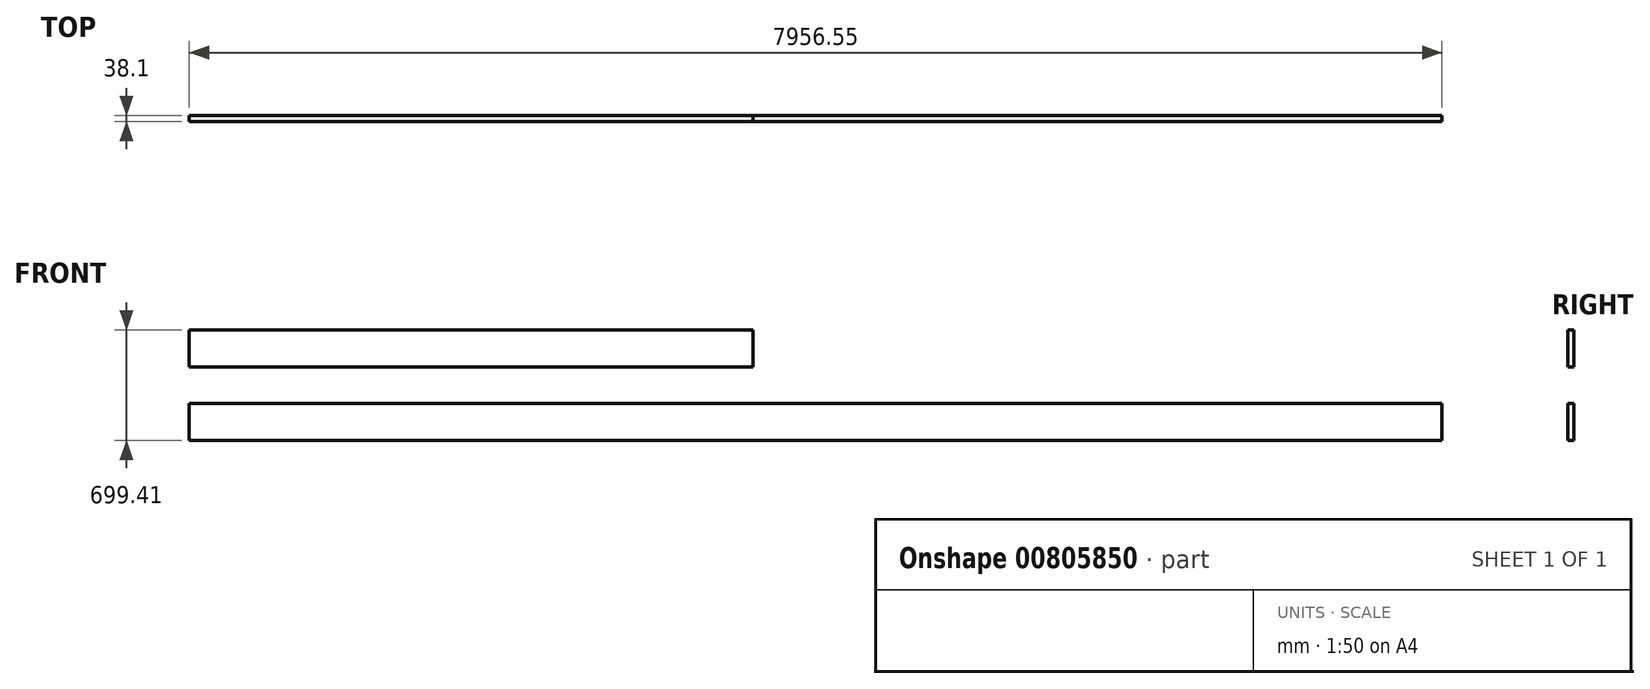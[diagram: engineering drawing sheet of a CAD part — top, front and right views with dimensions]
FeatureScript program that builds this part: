
annotation { "Feature Type Name" : "Feature", "Feature Type Description" : "" }
export const myFeature = defineFeature(function(context is Context, id is Id, definition is map)
    precondition{}
    {
        {
            var Q0;
            Q0=qCreatedBy(makeId("Front.planeOp"),FACE);
            var sketch = newSketch(context, id + "F0", { "sketchPlane" : qUnion([Q0])});
            skLineSegment(sketch, "E0.bottom", {"start": v(3581.4, 234.95) * mm, "end": v(0, 234.95) * mm});
            skLineSegment(sketch, "E0.top", {"start": v(3581.4, 0) * mm, "end": v(0, 0) * mm});
            skLineSegment(sketch, "E0.left", {"start": v(3581.4, 234.95) * mm, "end": v(3581.4, 0) * mm});
            skLineSegment(sketch, "E0.right", {"start": v(0, 234.95) * mm, "end": v(0, 0) * mm});
            skSolve(sketch);
        }
        {
            var Q0;
            Q0=qSketchRegion(id+"F0",true);
            extrude(context, id + "F1", {"entities" : qUnion([Q0]), "depth" : 38.1 * mm, "offsetDistance" : 25.4 * mm});
        }
        {
            var Q0;
            Q0=qCreatedBy(makeId("Front.planeOp"),FACE);
            var sketch = newSketch(context, id + "F2", { "sketchPlane" : qUnion([Q0])});
            skLineSegment(sketch, "E1.bottom", {"start": v(0, -229.5) * mm, "end": v(7956.55, -229.5) * mm});
            skLineSegment(sketch, "E1.top", {"start": v(0, -464.46) * mm, "end": v(7956.55, -464.46) * mm});
            skLineSegment(sketch, "E1.left", {"start": v(0, -229.5) * mm, "end": v(0, -464.46) * mm});
            skLineSegment(sketch, "E1.right", {"start": v(7956.55, -229.5) * mm, "end": v(7956.55, -464.46) * mm});
            skSolve(sketch);
        }
        {
            var Q0;
            Q0 = qSketchRegion(id + "F2", true);
            extrude(context, id + "F3", {"entities" : qUnion([Q0]), "depth" : 38.1 * mm, "offsetDistance" : 25.4 * mm});
        }
    });
